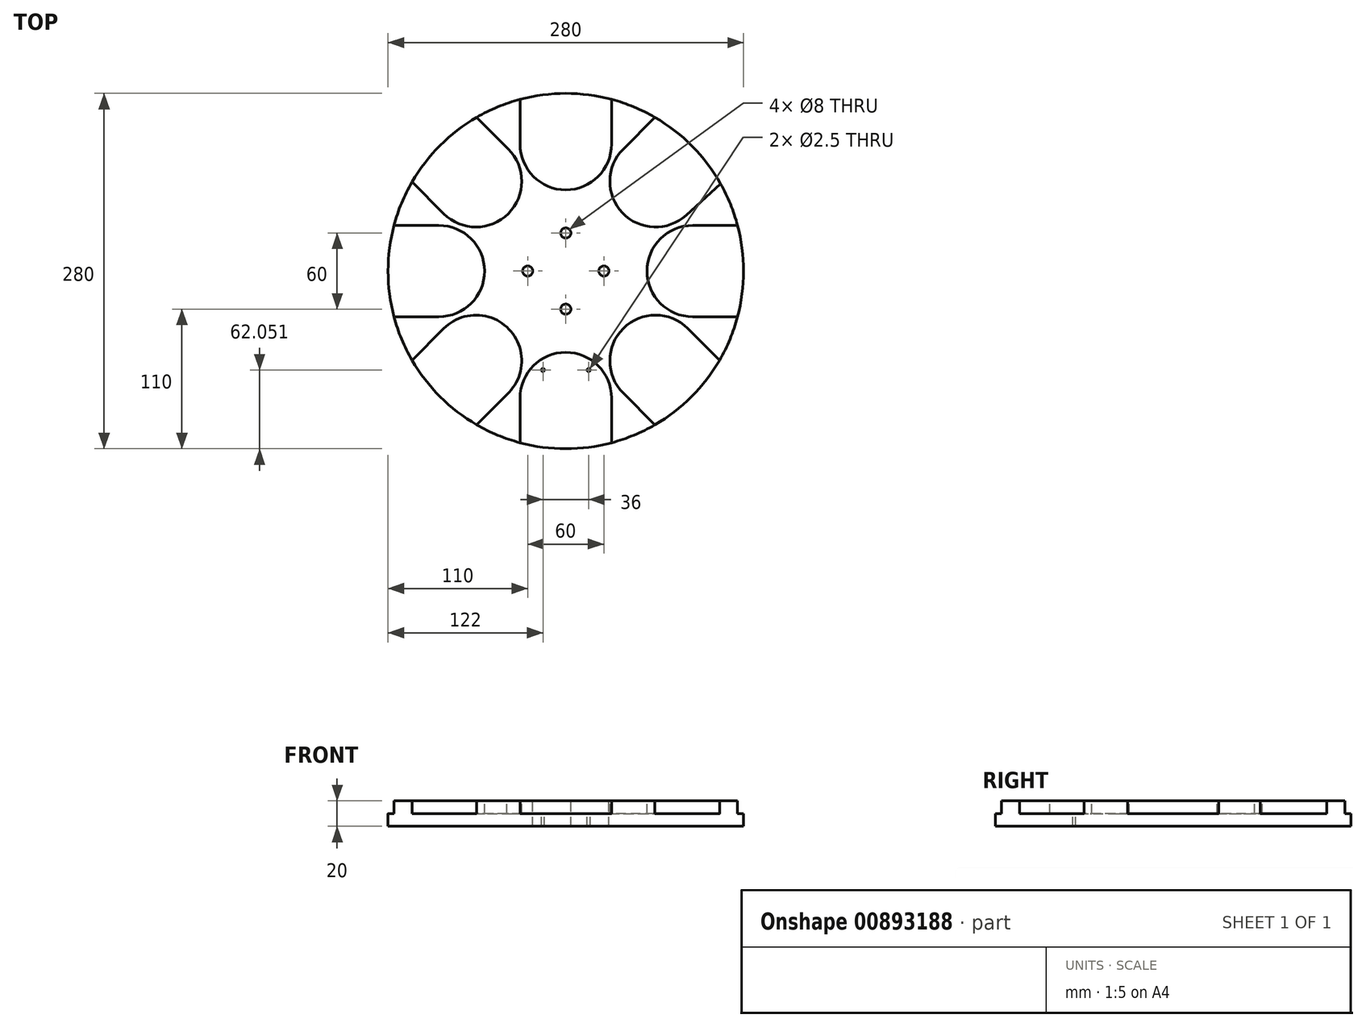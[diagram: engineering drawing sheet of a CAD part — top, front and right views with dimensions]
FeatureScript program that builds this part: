
annotation { "Feature Type Name" : "Feature", "Feature Type Description" : "" }
export const myFeature = defineFeature(function(context is Context, id is Id, definition is map)
    precondition{}
    {
        {
            var Q0;
            Q0=qCreatedBy(makeId("Top.planeOp"),FACE);
            var sketch = newSketch(context, id + "F0", { "sketchPlane" : qUnion([Q0])});
            skCircle(sketch, "E0", {"center": v(0, 0) * mm, "radius": 140 * mm});
            skSolve(sketch);
        }
        {
            var Q0;
            Q0=qSketchRegion(id+"F0",true);
            extrude(context, id + "F1", {"entities" : qUnion([Q0]), "depth" : 20 * mm, "offsetDistance" : 25 * mm});
        }
        {
            var Q0;
            Q0=makeQuery(id+"F1.opExtrude","CAP_FACE",FACE,{"disambiguationData":[OSD([sQuery(id+"F0.wireOp",EDGE,"E0")])],"isStart":false});
            var sketch = newSketch(context, id + "F2", { "sketchPlane" : qUnion([Q0])});
            skArc(sketch, "E1", {"start": v(-36, 100) * mm, "mid": v(0, 64) * mm, "end": v(36, 100) * mm});
            skCircle(sketch, "E2", {"center": v(0, 0) * mm, "radius": 100 * mm, "construction": true});
            skArc(sketch, "E3", {"start": v(45.25, 96.17) * mm, "mid": v(44.67, 45.86) * mm, "end": v(94.95, 44.1) * mm});
            skArc(sketch, "E4", {"start": v(-46.33, -97.2) * mm, "mid": v(-44.74, -45.79) * mm, "end": v(-96.17, -45.25) * mm});
            skArc(sketch, "E5", {"start": v(100, 36) * mm, "mid": v(64, 0) * mm, "end": v(100, -36) * mm});
            skArc(sketch, "E6", {"start": v(-100, -36) * mm, "mid": v(-64, 0) * mm, "end": v(-100, 36) * mm});
            skArc(sketch, "E7", {"start": v(36, -100) * mm, "mid": v(0, -64) * mm, "end": v(-36, -100) * mm});
            skArc(sketch, "E8", {"start": v(96.17, -45.25) * mm, "mid": v(45.25, -45.25) * mm, "end": v(45.25, -96.17) * mm});
            skArc(sketch, "E9", {"start": v(-96.17, 45.25) * mm, "mid": v(-45.25, 45.25) * mm, "end": v(-45.25, 96.17) * mm});
            skLineSegment(sketch, "E10", {"start": v(0, 100) * mm, "end": v(0, -100) * mm, "construction": true});
            skLineSegment(sketch, "E11", {"start": v(-70.71, 70.71) * mm, "end": v(70.71, -70.71) * mm, "construction": true});
            skLineSegment(sketch, "E12", {"start": v(-100, 0) * mm, "end": v(100, 0) * mm, "construction": true});
            skLineSegment(sketch, "E13", {"start": v(-70.71, -70.71) * mm, "end": v(70.71, 70.71) * mm, "construction": true});
            skLineSegment(sketch, "E14", {"start": v(-96.17, -45.25) * mm, "end": v(-121.12, -70.21) * mm});
            skLineSegment(sketch, "E15", {"start": v(-46.33, -97.2) * mm, "end": v(-70.24, -121.1) * mm});
            skArc(sketch, "E16", {"start": v(-36, -135.3) * mm, "mid": v(0, -140) * mm, "end": v(36, -135.3) * mm});
            skLineSegment(sketch, "E17", {"start": v(-36, -100) * mm, "end": v(-36, -135.3) * mm});
            skLineSegment(sketch, "E18", {"start": v(36, -100) * mm, "end": v(36, -135.3) * mm});
            skLineSegment(sketch, "E19", {"start": v(45.25, -96.17) * mm, "end": v(70.21, -121.12) * mm});
            skLineSegment(sketch, "E20", {"start": v(96.17, -45.25) * mm, "end": v(121.12, -70.21) * mm});
            skLineSegment(sketch, "E21", {"start": v(100, -36) * mm, "end": v(135.3, -36) * mm});
            skLineSegment(sketch, "E22", {"start": v(100, 36) * mm, "end": v(135.3, 36) * mm});
            skLineSegment(sketch, "E23", {"start": v(-100, -36) * mm, "end": v(-135.3, -36) * mm});
            skLineSegment(sketch, "E24", {"start": v(-100, 36) * mm, "end": v(-135.3, 36) * mm});
            skLineSegment(sketch, "E25", {"start": v(-96.17, 45.25) * mm, "end": v(-121.12, 70.21) * mm});
            skLineSegment(sketch, "E26", {"start": v(-40.51, 91.43) * mm, "end": v(-70.21, 121.12) * mm});
            skLineSegment(sketch, "E27", {"start": v(-36, 100) * mm, "end": v(-36, 135.3) * mm});
            skLineSegment(sketch, "E28", {"start": v(36, 100) * mm, "end": v(36, 135.3) * mm});
            skLineSegment(sketch, "E29", {"start": v(45.25, 96.17) * mm, "end": v(70.21, 121.12) * mm});
            skLineSegment(sketch, "E30", {"start": v(94.95, 44.1) * mm, "end": v(121.98, 68.71) * mm});
            skArc(sketch, "E31.trimOffspring", {"start": v(70.21, -121.12) * mm, "mid": v(99, -99) * mm, "end": v(121.12, -70.21) * mm});
            skArc(sketch, "E32.trimOffspring", {"start": v(135.3, -36) * mm, "mid": v(140, 0) * mm, "end": v(135.3, 36) * mm});
            skArc(sketch, "E33.trimOffspring", {"start": v(121.98, 68.71) * mm, "mid": v(99.6, 98.38) * mm, "end": v(70.21, 121.12) * mm});
            skArc(sketch, "E34.trimOffspring", {"start": v(36, 135.3) * mm, "mid": v(0, 140) * mm, "end": v(-36, 135.3) * mm});
            skArc(sketch, "E35.trimOffspring", {"start": v(-70.21, 121.12) * mm, "mid": v(-99, 99) * mm, "end": v(-121.12, 70.21) * mm});
            skArc(sketch, "E36.trimOffspring", {"start": v(-135.3, 36) * mm, "mid": v(-140, 0) * mm, "end": v(-135.3, -36) * mm});
            skArc(sketch, "E37.trimOffspring", {"start": v(-121.12, -70.21) * mm, "mid": v(-99, -98.98) * mm, "end": v(-70.24, -121.1) * mm});
            skSolve(sketch);
        }
        {
            var Q0;
            Q0=qSketchRegion(id+"F2",true);
            extrude(context, id + "F3", {"entities" : qUnion([Q0]), "operationType" : NewBodyOperationType.REMOVE, "oppositeDirection" : true, "depth" : 10 * mm, "offsetDistance" : 25 * mm});
        }
        {
            var Q0;
            Q0=makeQuery(id+"F3.boolean.opBoolean","COPY",FACE,{"derivedFrom":makeQuery(id+"F3.opExtrude","CAP_FACE",FACE,{"disambiguationData":[OSD([sQuery(id+"F2.wireOp",EDGE,"E7"),sQuery(id+"F2.wireOp",EDGE,"E16"),sQuery(id+"F2.wireOp",EDGE,"E17"),sQuery(id+"F2.wireOp",EDGE,"E18")])],"isStart":false})});
            var sketch = newSketch(context, id + "F4", { "sketchPlane" : qUnion([Q0])});
            skCircle(sketch, "E38", {"center": v(0, 0) * mm, "radius": 80 * mm, "construction": true});
            skCircle(sketch, "E39", {"center": v(-18, -77.95) * mm, "radius": 1.25 * mm});
            skCircle(sketch, "E40", {"center": v(18, -77.95) * mm, "radius": 1.25 * mm});
            skCircle(sketch, "E41", {"center": v(0, -100) * mm, "radius": 24 * mm, "construction": true});
            skCircle(sketch, "E42", {"center": v(0, 0) * mm, "radius": 50 * mm, "construction": true});
            skCircle(sketch, "E43", {"center": v(50, 0) * mm, "radius": 4 * mm});
            skCircle(sketch, "E44", {"center": v(0, -50) * mm, "radius": 4 * mm});
            skCircle(sketch, "E45", {"center": v(-50, 0) * mm, "radius": 4 * mm});
            skCircle(sketch, "E46", {"center": v(0, 50) * mm, "radius": 4 * mm});
            skSolve(sketch);
        }
        {
            var Q0;
            Q0=makeQuery(id+"F4.imprint","IMPRINT",FACE,{"disambiguationData":[TD([[makeQuery(id+"F4.imprint","IMPRINT",EDGE,{"derivedFrom":sQuery(id+"F4.wireOp",EDGE,"E39")}),1.0]])]});
            var Q1;
            Q1=makeQuery(id+"F4.imprint","IMPRINT",FACE,{"disambiguationData":[TD([[makeQuery(id+"F4.imprint","IMPRINT",EDGE,{"derivedFrom":sQuery(id+"F4.wireOp",EDGE,"E40")}),1.0]])]});
            extrude(context, id + "F5", {"entities" : qUnion([Q0, Q1]), "operationType" : NewBodyOperationType.REMOVE, "endBound" : BoundingType.THROUGH_ALL, "oppositeDirection" : true, "depth" : 25 * mm, "offsetDistance" : 25 * mm});
        }
        {
            var Q0;
            Q0=makeQuery(id+"F1.opExtrude","CAP_FACE",FACE,{"disambiguationData":[OSD([sQuery(id+"F0.wireOp",EDGE,"E0")])],"isStart":false});
            var sketch = newSketch(context, id + "F6", { "sketchPlane" : qUnion([Q0])});
            skCircle(sketch, "E47", {"center": v(0, 0) * mm, "radius": 30 * mm, "construction": true});
            skCircle(sketch, "E48", {"center": v(30, 0) * mm, "radius": 4 * mm});
            skCircle(sketch, "E49", {"center": v(0, -30) * mm, "radius": 4 * mm});
            skCircle(sketch, "E50", {"center": v(-30, 0) * mm, "radius": 4 * mm});
            skCircle(sketch, "E51", {"center": v(0, 30) * mm, "radius": 4 * mm});
            skSolve(sketch);
        }
        {
            var Q0;
            Q0 = qSketchRegion(id + "F6", true);
            extrude(context, id + "F7", {"entities" : qUnion([Q0]), "operationType" : NewBodyOperationType.REMOVE, "endBound" : BoundingType.THROUGH_ALL, "oppositeDirection" : true, "depth" : 25 * mm, "offsetDistance" : 25 * mm});
        }
    });
